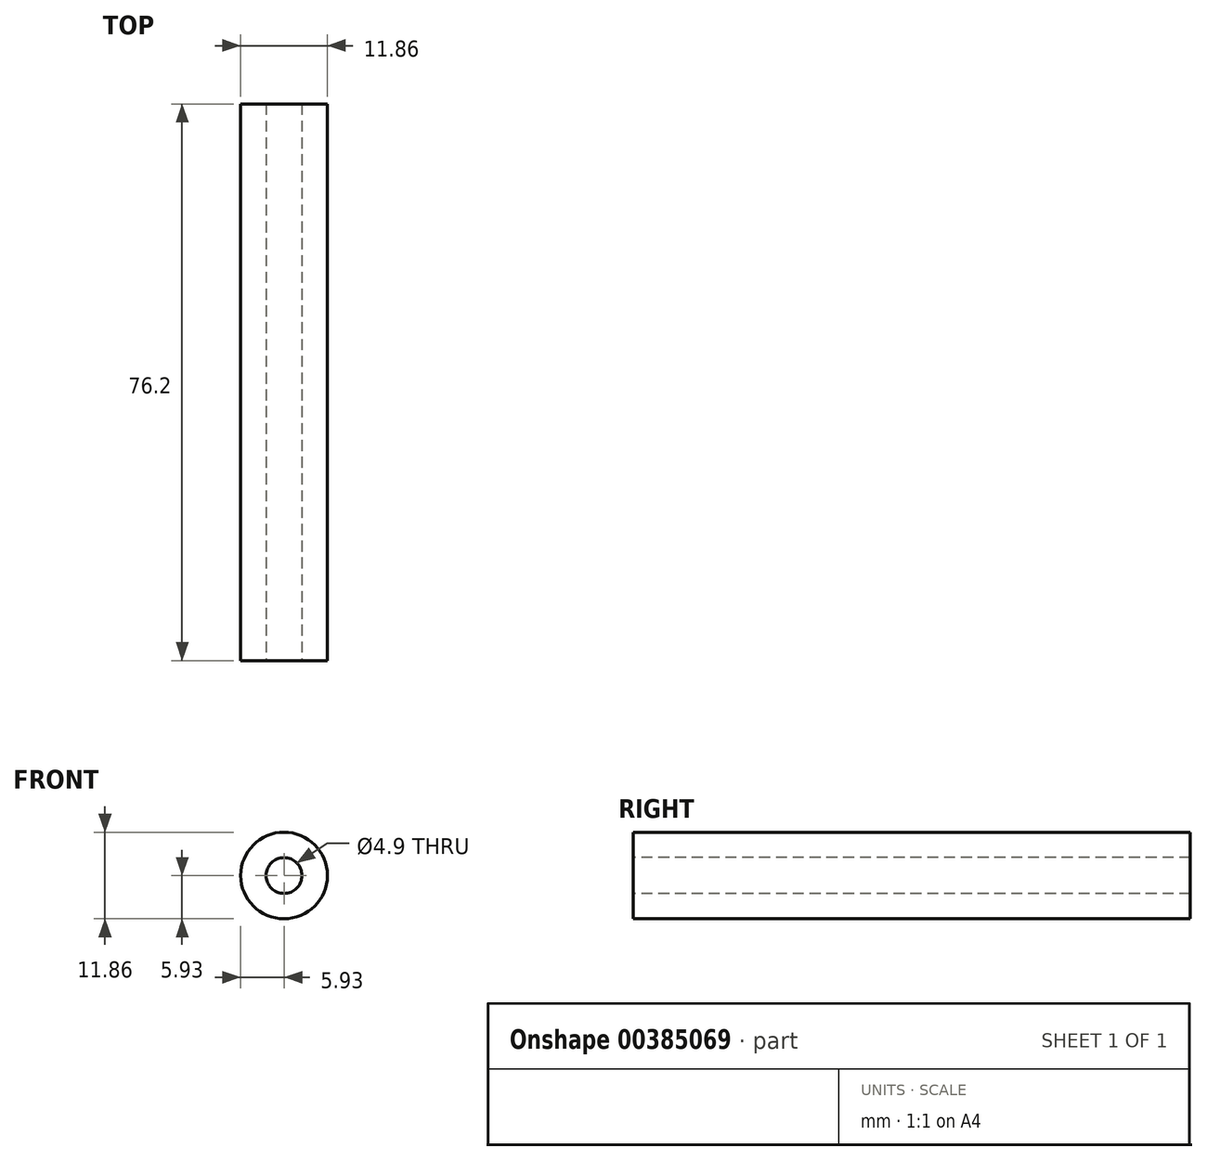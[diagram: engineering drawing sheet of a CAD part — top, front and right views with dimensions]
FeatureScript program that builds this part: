
annotation { "Feature Type Name" : "Feature", "Feature Type Description" : "" }
export const myFeature = defineFeature(function(context is Context, id is Id, definition is map)
    precondition{}
    {
        {
            var Q0;
            Q0=qCreatedBy(makeId("Front.planeOp"),FACE);
            var sketch = newSketch(context, id + "F0", { "sketchPlane" : qUnion([Q0])});
            skCircle(sketch, "E0", {"center": v(0, 0) * mm, "radius": 2.45 * mm});
            skCircle(sketch, "E1", {"center": v(0, 0) * mm, "radius": 5.93 * mm});
            skLineSegment(sketch, "E2", {"start": v(0, 2.45) * mm, "end": v(0, 5.93) * mm});
            skLineSegment(sketch, "E3", {"start": v(-2.45, 0) * mm, "end": v(-5.93, 0) * mm});
            skLineSegment(sketch, "E4", {"start": v(0, -2.45) * mm, "end": v(0, -5.93) * mm});
            skLineSegment(sketch, "E5", {"start": v(5.93, 0) * mm, "end": v(2.45, 0) * mm});
            skSolve(sketch);
        }
        {
            var Q0;
            {var subQ0=sQuery(id+"F0.wireOp",EDGE,"E2");Q0=makeQuery(id+"F0.imprint","IMPRINT",FACE,{"disambiguationData":[TD([[makeQuery(id+"F0.imprint","IMPRINT",EDGE,{"derivedFrom":subQ0}),1.0]])]});}
            var Q1;
            {var subQ0=sQuery(id+"F0.wireOp",EDGE,"E2");Q1=makeQuery(id+"F0.imprint","IMPRINT",FACE,{"disambiguationData":[TD([[makeQuery(id+"F0.imprint","IMPRINT",EDGE,{"derivedFrom":subQ0}),-1.0]])]});}
            var Q2;
            {var subQ0=sQuery(id+"F0.wireOp",EDGE,"E3");Q2=makeQuery(id+"F0.imprint","IMPRINT",FACE,{"disambiguationData":[TD([[makeQuery(id+"F0.imprint","IMPRINT",EDGE,{"derivedFrom":subQ0}),1.0]])]});}
            var Q3;
            {var subQ0=sQuery(id+"F0.wireOp",EDGE,"E4");Q3=makeQuery(id+"F0.imprint","IMPRINT",FACE,{"disambiguationData":[TD([[makeQuery(id+"F0.imprint","IMPRINT",EDGE,{"derivedFrom":subQ0}),1.0]])]});}
            var Q4;
            Q4=sQuery(id+"F0.wireOp",EDGE,"E0");
            extrude(context, id + "F1", {"entities" : qUnion([Q0, Q1, Q2, Q3]), "surfaceEntities" : qUnion([Q4]), "oppositeDirection" : true, "depth" : 76.2 * mm});
        }
    });
